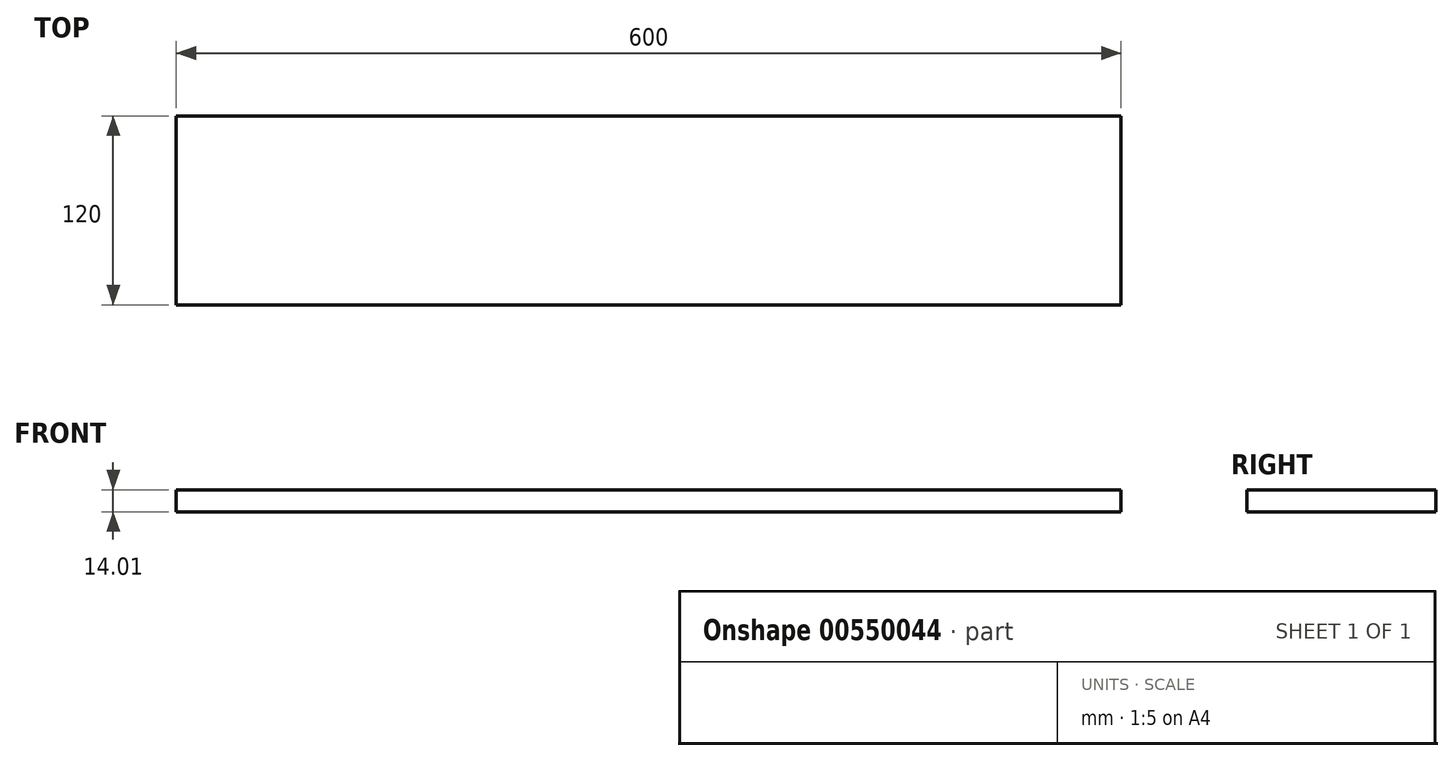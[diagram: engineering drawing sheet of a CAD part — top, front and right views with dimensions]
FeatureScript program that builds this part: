
annotation { "Feature Type Name" : "Feature", "Feature Type Description" : "" }
export const myFeature = defineFeature(function(context is Context, id is Id, definition is map)
    precondition{}
    {
        {
            var Q0;
            Q0=qCreatedBy(makeId("Right.planeOp"),FACE);
            var sketch = newSketch(context, id + "F0", { "sketchPlane" : qUnion([Q0])});
            skLineSegment(sketch, "E0.bottom", {"start": v(0, 0) * mm, "end": v(120, 0) * mm});
            skLineSegment(sketch, "E0.top", {"start": v(0, 14.01) * mm, "end": v(120, 14.01) * mm});
            skLineSegment(sketch, "E0.left", {"start": v(0, 0) * mm, "end": v(0, 14.01) * mm});
            skLineSegment(sketch, "E0.right", {"start": v(120, 0) * mm, "end": v(120, 14.01) * mm});
            skSolve(sketch);
        }
        {
            var Q0;
            Q0 = qSketchRegion(id + "F0", true);
            extrude(context, id + "F1", {"entities" : qUnion([Q0]), "depth" : 600 * mm, "offsetDistance" : 25.4 * mm});
        }
    });
